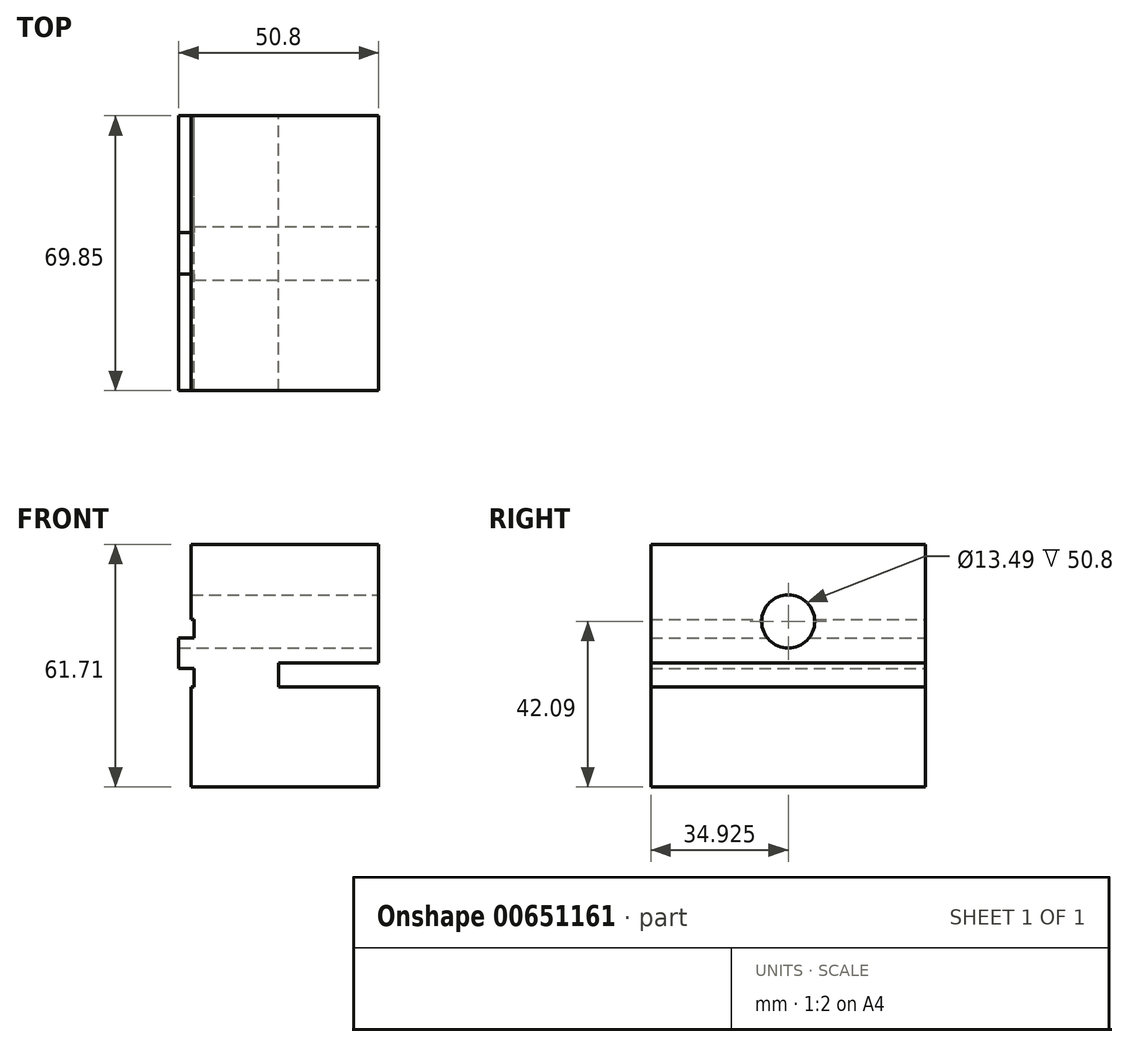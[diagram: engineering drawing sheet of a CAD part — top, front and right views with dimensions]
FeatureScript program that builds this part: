
annotation { "Feature Type Name" : "Feature", "Feature Type Description" : "" }
export const myFeature = defineFeature(function(context is Context, id is Id, definition is map)
    precondition{}
    {
        {
            var Q0;
            Q0=qCreatedBy(makeId("Front.planeOp"),FACE);
            var sketch = newSketch(context, id + "F0", { "sketchPlane" : qUnion([Q0])});
            skLineSegment(sketch, "E0", {"start": v(-47.63, -42.09) * mm, "end": v(-47.63, -16.69) * mm});
            skLineSegment(sketch, "E1", {"start": v(0, -42.09) * mm, "end": v(-47.63, -42.09) * mm});
            skLineSegment(sketch, "E2", {"start": v(0, -42.09) * mm, "end": v(0, -16.69) * mm});
            skLineSegment(sketch, "E3", {"start": v(0, -16.69) * mm, "end": v(-25.4, -16.69) * mm});
            skLineSegment(sketch, "E4", {"start": v(-47.63, -16.69) * mm, "end": v(-46.84, -16.69) * mm});
            skLineSegment(sketch, "E5", {"start": v(-46.84, -16.69) * mm, "end": v(-46.84, -11.91) * mm});
            skLineSegment(sketch, "E6", {"start": v(-46.84, -11.91) * mm, "end": v(-50.8, -11.91) * mm});
            skLineSegment(sketch, "E7", {"start": v(-50.8, -11.91) * mm, "end": v(-50.8, -4.2) * mm});
            skLineSegment(sketch, "E8", {"start": v(-50.8, -4.2) * mm, "end": v(-46.84, -4.2) * mm});
            skLineSegment(sketch, "E9", {"start": v(-46.84, -4.2) * mm, "end": v(-46.84, 0.57) * mm});
            skLineSegment(sketch, "E10", {"start": v(-46.84, 0.57) * mm, "end": v(-47.63, 0.57) * mm});
            skLineSegment(sketch, "E11", {"start": v(-47.63, 0.57) * mm, "end": v(-47.63, 19.62) * mm});
            skLineSegment(sketch, "E12", {"start": v(-47.63, 19.62) * mm, "end": v(0, 19.62) * mm});
            skLineSegment(sketch, "E13", {"start": v(0, 19.62) * mm, "end": v(0, -10.56) * mm});
            skLineSegment(sketch, "E14", {"start": v(0, -10.56) * mm, "end": v(-25.4, -10.56) * mm});
            skLineSegment(sketch, "E15", {"start": v(-25.4, -16.69) * mm, "end": v(-25.4, -10.56) * mm});
            skSolve(sketch);
        }
        {
            var Q0;
            Q0=makeQuery(id+"F0.imprint","IMPRINT",FACE,{"disambiguationData":[TD([[makeQuery(id+"F0.imprint","IMPRINT",EDGE,{"derivedFrom":sQuery(id+"F0.wireOp",EDGE,"E0")}),-1.0]])]});
            extrude(context, id + "F1", {"entities" : qUnion([Q0]), "depth" : 69.85 * mm, "offsetDistance" : 25.4 * mm});
        }
        {
            var Q0;
            Q0=makeQuery(id+"F1.opExtrude","SWEPT_FACE",FACE,{"disambiguationData":[OSD([sQuery(id+"F0.wireOp",EDGE,"E13")])]});
            var sketch = newSketch(context, id + "F2", { "sketchPlane" : qUnion([Q0])});
            skCircle(sketch, "E16", {"center": v(-34.92, 0) * mm, "radius": 6.74 * mm});
            skSolve(sketch);
        }
        {
            var Q0;
            Q0=sQuery(id+"F2.wireOp",VERTEX,"E16.center");
            var Q1;
            Q1=makeQuery(id+"F1.opExtrude","SWEPT_BODY",BODY,{"disambiguationData":[OSD([sQuery(id+"F0.wireOp",EDGE,"E0"),sQuery(id+"F0.wireOp",EDGE,"E1"),sQuery(id+"F0.wireOp",EDGE,"E2"),sQuery(id+"F0.wireOp",EDGE,"E3"),sQuery(id+"F0.wireOp",EDGE,"E4"),sQuery(id+"F0.wireOp",EDGE,"E5"),sQuery(id+"F0.wireOp",EDGE,"E6"),sQuery(id+"F0.wireOp",EDGE,"E7"),sQuery(id+"F0.wireOp",EDGE,"E8"),sQuery(id+"F0.wireOp",EDGE,"E9"),sQuery(id+"F0.wireOp",EDGE,"E10"),sQuery(id+"F0.wireOp",EDGE,"E11"),sQuery(id+"F0.wireOp",EDGE,"E12"),sQuery(id+"F0.wireOp",EDGE,"E13"),sQuery(id+"F0.wireOp",EDGE,"E14"),sQuery(id+"F0.wireOp",EDGE,"E15")])]});
            hole(context, id + "F3", {"style" : HoleStyle.SIMPLE, "endStyle" : HoleEndStyle.THROUGH, "holeDiameter" : 13.5 * mm, "majorDiameter" : 6.35 * mm, "isTappedThrough" : true, "tappedDepth" : 12.7 * mm, "tapClearance" : 3, "locations" : qUnion([Q0]), "scope" : qUnion([Q1])});
        }
    });
